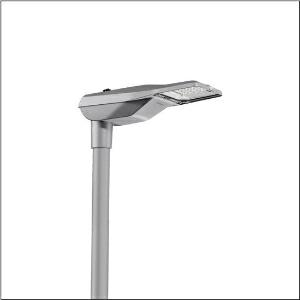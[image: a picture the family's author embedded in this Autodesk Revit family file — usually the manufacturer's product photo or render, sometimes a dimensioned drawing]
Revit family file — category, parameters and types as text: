
# Revit family: streetlight_sl_21_iq_micro___p0_5a_5xe1v31v08cb_beee
name_source: partatom
category: Lighting Fixtures
units: mm (PartAtom-declared; Revit-internal decimal feet)

## family parameters
Cut with Voids When Loaded = No
Host = Face
Light Source = No
Part Type = Normal
Room Calculation Point = No
Round Connector Dimension = Use Diameter
Shared = No

## types (1)
- --- (1 x LED, 2840 lm, 19.1 W, 3000K)
    Apparent Load = 19 VA
    CIE Flux Codes = 37 73 96 100 100
    Color Rendering = 70
    Color Temperature = 3000K
    Default Elevation = 1800 mm
    Description = Streetlight SL 21 iQ micro, mast luminaire, primary light control with lens, of PMMA, primary optical cover: cover, of toughened safety glass, transparent, light distribution: P0.5a, light emission: direct distribution, primary light characteristic: asymmetric, installation type: post-top, side-entry, LED, High Power LED, rated luminous flux: 2.840lm, luminous efficacy: 149lm/W, light colour: 730, colour temperature: 3000K, control gear: iQ-Street Remote, D4i with power reduction, control: pre-setting: logarithmic dimming characteristic, Street-Remote, Auto-Match, Temp-Guard, Lumen-Switch, Night-Set, Smart-Wire, Light-Fading, Desk-Remote (wireless, voltage-free reading and setting of iQ features in the workshop via application-optimized NFC function/RFID function), optimised constant luminous flux control (CLO 2.0), mains connection: 220..240V, AC, 50/60Hz, start of lifetime: 19W, end of service life: 20W, reduction: 9W, luminaire housing, of diecast aluminium, powder-coated, SITECO metallic grey (DB 702S), corrosivity category C5 high according to DIN EN ISO 12944, please order mast flange separately, inclination adjustable: 0°, 5°, 10°, 15°, sealing non-destructively replaceable, multi-level sealing system, length: 528mm, width: 235mm, height: 110mm, mast flange for spigot size: 42mm (side-entry): 5XC10008XM4, 60/48mm (side-entry/post-top): 5XC10108XM2, 76/60mm (side-entry/post-top): 5XC10108XM1, mounting height: 4..8m, Smart Interface above, protection rating (complete): IP66, insulation class (complete): insulation class II (safety insulation), certification: CE, ENEC, ENEC+, VDE, impact resistance: IK10, permissible operating ambient temperature for outdoor applications: -40..+50°C, standard-compliant lighting for roads and squares, packaging unit: 1 piece

Light Distribution: P0.5a
    Height = 110 mm
    Lamp = 1 x LED
    Lamp Light Flux = 2840 lm
    Lamp Power = 19.1 W
    Lamp count = 1
    Length = 528 mm
    Luminous efficacy = 149 lm/W
    Manufacturer = Siteco
    ModVariant = No
    Model = 5XE1V31V08CB
    Mounting Place = Pole
    Mounting Type = Pole top
    Number of Poles = 1
    OnlyDefault = Yes
    Power Factor = 1
    Product Name = Streetlight SL 21 iQ micro | P0.5a
    Product group = mast luminaire | pylon top
    ProductGroupID = 6100
    Protection Class = Protection class II
    Protection Degree = IP 66
    RLX_Detail_Level = 1
    RLX_Emergency_Light_Flux = 0 lm
    RLX_Emergency_Type = 0
    RLX_Emergency_Type_DB = No
    RlxData = <blob elided: 97645 chars, md5=37196edb>
    Socket = socket
    Standby Power = 0 W
    System Light Flux = 2840 lm
    System Power = 19 W
    Type Comments = factory setting: luminous flux: 100 % | dim-lin: 254 | 387 mA
    Type Image = l_1277292.jpg
    URL = http://relux.com
    VarID = @adj_079521
    Voltage = 0 V
    Weight = 0.00 kg
    Width = 235 mm

## geometry (parser evidence)
native form markers: Blend x4, Sweep x10
no freeform markers — native parametric forms only
